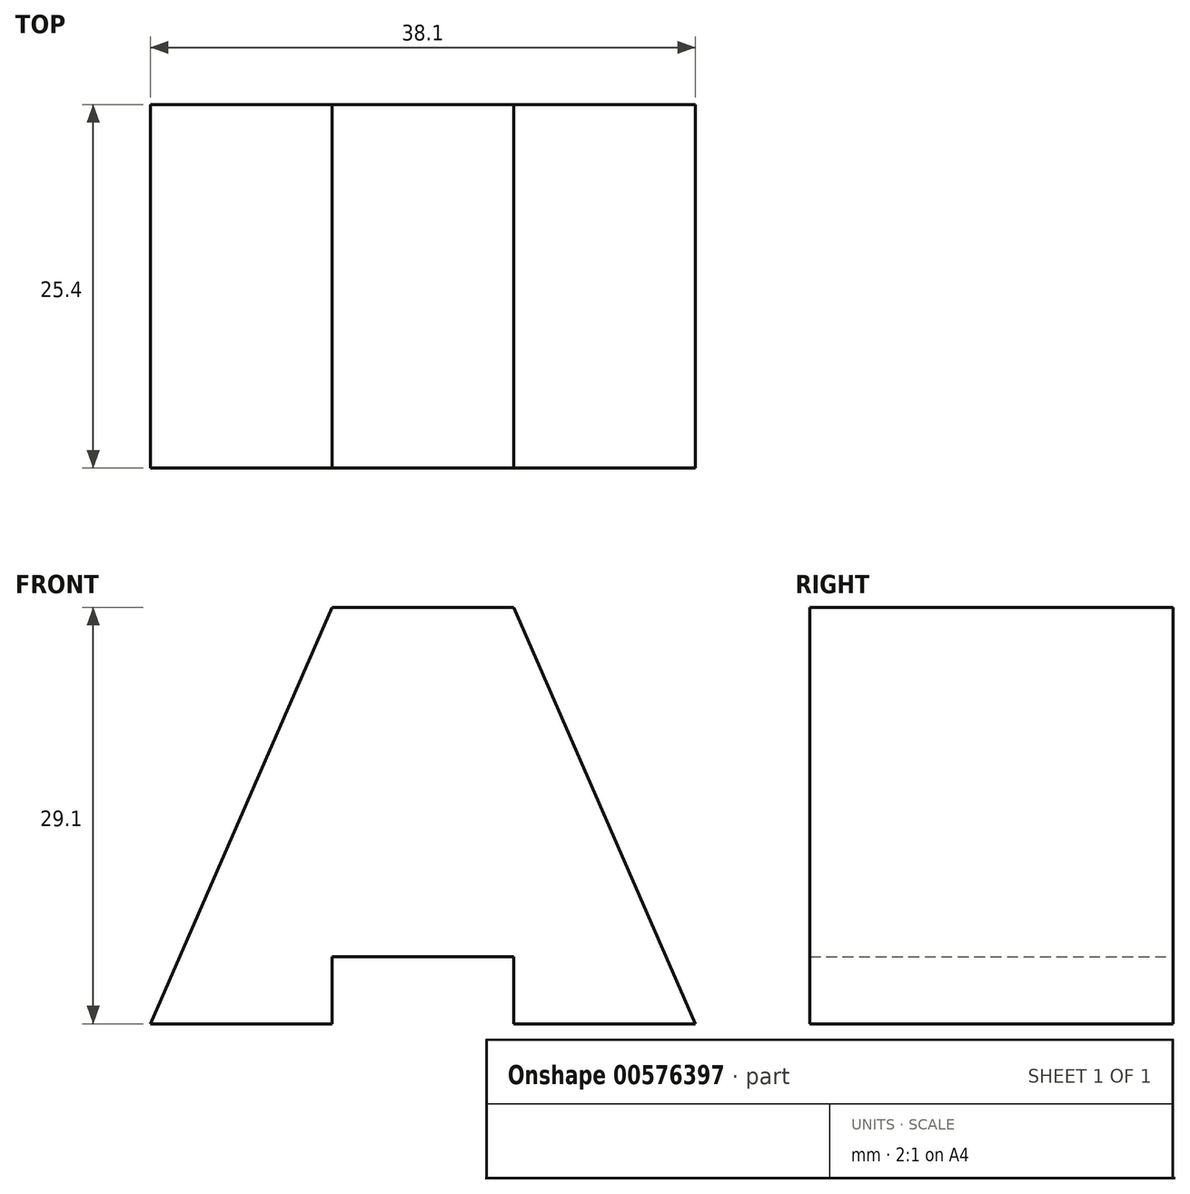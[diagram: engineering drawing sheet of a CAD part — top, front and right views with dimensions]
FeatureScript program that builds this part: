
annotation { "Feature Type Name" : "Feature", "Feature Type Description" : "" }
export const myFeature = defineFeature(function(context is Context, id is Id, definition is map)
    precondition{}
    {
        {
            var Q0;
            Q0=qCreatedBy(makeId("Front.planeOp"),FACE);
            var sketch = newSketch(context, id + "F0", { "sketchPlane" : qUnion([Q0])});
            skLineSegment(sketch, "E0", {"start": v(-41.98, 49.9) * mm, "end": v(-29.28, 49.9) * mm});
            skLineSegment(sketch, "E1", {"start": v(-29.28, 49.9) * mm, "end": v(-16.58, 20.8) * mm});
            skLineSegment(sketch, "E2", {"start": v(-16.58, 20.8) * mm, "end": v(-29.28, 20.8) * mm});
            skLineSegment(sketch, "E3", {"start": v(-29.28, 20.8) * mm, "end": v(-29.28, 25.47) * mm});
            skLineSegment(sketch, "E4", {"start": v(-29.28, 25.47) * mm, "end": v(-41.98, 25.47) * mm});
            skLineSegment(sketch, "E5", {"start": v(-41.98, 25.47) * mm, "end": v(-41.98, 20.8) * mm});
            skLineSegment(sketch, "E6", {"start": v(-41.98, 20.8) * mm, "end": v(-54.68, 20.8) * mm});
            skLineSegment(sketch, "E7", {"start": v(-54.68, 20.8) * mm, "end": v(-41.98, 49.9) * mm});
            skSolve(sketch);
        }
        {
            var Q0;
            Q0 = qSketchRegion(id + "F0", true);
            extrude(context, id + "F1", {"entities" : qUnion([Q0]), "depth" : 25.4 * mm, "offsetDistance" : 25.4 * mm});
        }
    });
